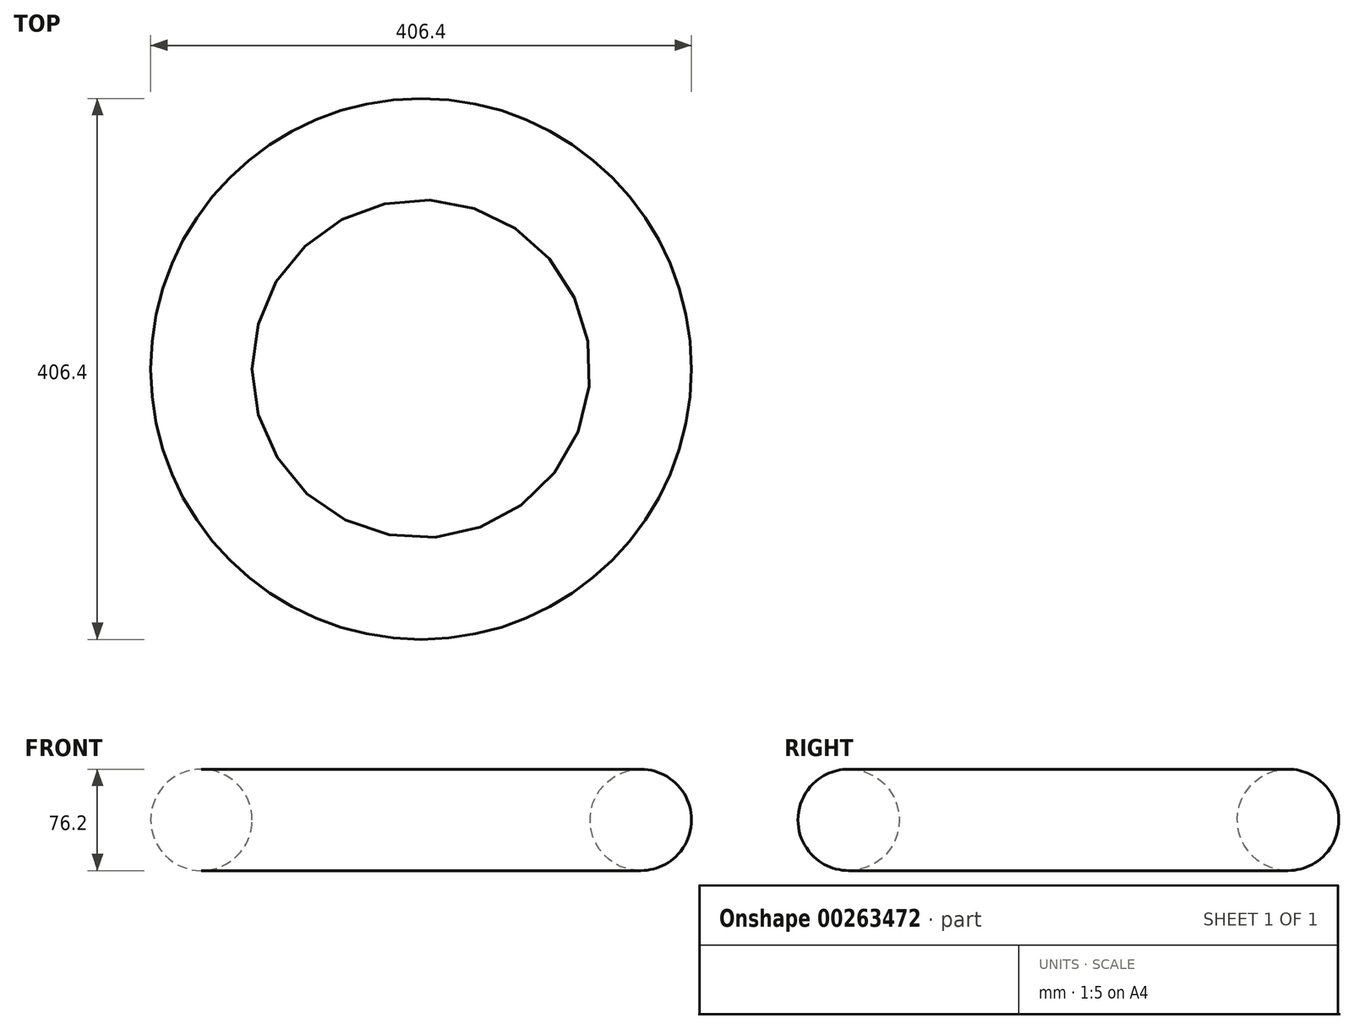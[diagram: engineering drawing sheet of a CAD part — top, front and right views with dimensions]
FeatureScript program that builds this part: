
annotation { "Feature Type Name" : "Feature", "Feature Type Description" : "" }
export const myFeature = defineFeature(function(context is Context, id is Id, definition is map)
    precondition{}
    {
        {
            var Q0;
            Q0=qCreatedBy(makeId("Front.planeOp"),FACE);
            var sketch = newSketch(context, id + "F0", { "sketchPlane" : qUnion([Q0])});
            skCircle(sketch, "E0", {"center": v(-165.1, 0) * mm, "radius": 38.1 * mm});
            skSolve(sketch);
        }
        {
            var Q0;
            Q0=qCreatedBy(makeId("Front.planeOp"),FACE);
            var sketch = newSketch(context, id + "F1", { "sketchPlane" : qUnion([Q0])});
            skLineSegment(sketch, "E1", {"start": v(0, 77.4) * mm, "end": v(0, -75.41) * mm});
            skSolve(sketch);
        }
        {
            var Q0;
            Q0=sQuery(id+"F0.wireOp",EDGE,"E0");
            var Q1;
            Q1=sQuery(id+"F1.wireOp",EDGE,"E1");
            revolve(context, id + "F2", {"bodyType" : ToolBodyType.SURFACE, "surfaceEntities" : qUnion([Q0]), "axis" : qUnion([Q1]), "revolveType" : RevolveType.FULL});
        }
    });
